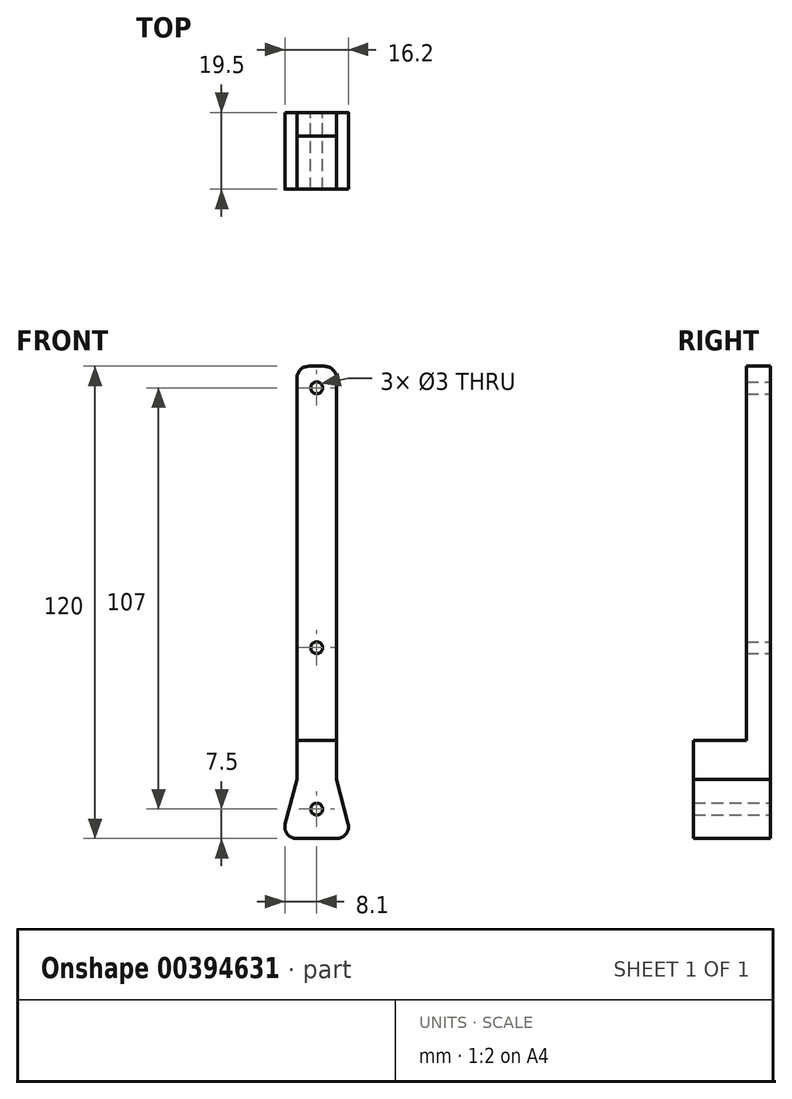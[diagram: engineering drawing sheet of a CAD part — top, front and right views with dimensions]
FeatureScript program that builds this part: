
annotation { "Feature Type Name" : "Feature", "Feature Type Description" : "" }
export const myFeature = defineFeature(function(context is Context, id is Id, definition is map)
    precondition{}
    {
        {
            var Q0;
            Q0=qCreatedBy(makeId("Front.planeOp"),FACE);
            var sketch = newSketch(context, id + "F0", { "sketchPlane" : qUnion([Q0])});
            skLineSegment(sketch, "E0", {"start": v(0, 0) * mm, "end": v(9, 0) * mm});
            skLineSegment(sketch, "E1", {"start": v(-1.18, 15) * mm, "end": v(3.08, 15) * mm, "construction": true});
            skLineSegment(sketch, "E2", {"start": v(5, 15) * mm, "end": v(9, 0) * mm});
            skLineSegment(sketch, "E3", {"start": v(5, 15) * mm, "end": v(5, 25) * mm});
            skLineSegment(sketch, "E4", {"start": v(5, 25) * mm, "end": v(0, 25) * mm});
            skLineSegment(sketch, "E5", {"start": v(0, 25) * mm, "end": v(0, 0) * mm});
            skLineSegment(sketch, "E6.MirrorCS", {"start": v(-5, 25) * mm, "end": v(0, 25) * mm});
            skLineSegment(sketch, "E7.MirrorCS", {"start": v(-5, 15) * mm, "end": v(-5, 25) * mm});
            skLineSegment(sketch, "E8.MirrorCS", {"start": v(-5, 15) * mm, "end": v(-9, 0) * mm});
            skLineSegment(sketch, "E9.MirrorCS", {"start": v(0, 0) * mm, "end": v(-9, 0) * mm});
            skLineSegment(sketch, "E10", {"start": v(7, 7.5) * mm, "end": v(-7, 7.5) * mm, "construction": true});
            skLineSegment(sketch, "E11.bottom", {"start": v(-5, 25) * mm, "end": v(5, 25) * mm});
            skLineSegment(sketch, "E11.top", {"start": v(-5, 120) * mm, "end": v(5, 120) * mm});
            skLineSegment(sketch, "E11.left", {"start": v(-5, 25) * mm, "end": v(-5, 120) * mm});
            skLineSegment(sketch, "E11.right", {"start": v(5, 25) * mm, "end": v(5, 120) * mm});
            skCircle(sketch, "E12", {"center": v(0, 7.5) * mm, "radius": 1.5 * mm});
            skCircle(sketch, "E13", {"center": v(0, 48.5) * mm, "radius": 1.5 * mm});
            skCircle(sketch, "E14", {"center": v(0, 114.5) * mm, "radius": 1.5 * mm});
            skSolve(sketch);
        }
        {
            var Q0;
            {var subQ1=sQuery(id+"F0.wireOp",EDGE,"E5");Q0=makeQuery(id+"F0.imprint","IMPRINT",FACE,{"disambiguationData":[TD([[makeQuery(id+"F0.imprint","IMPRINT",EDGE,{"derivedFrom":subQ1}),-1.0]])]});}
            var Q1;
            Q1=makeQuery(id+"F0.imprint","IMPRINT",FACE,{"disambiguationData":[TD([[makeQuery(id+"F0.imprint","IMPRINT",EDGE,{"derivedFrom":sQuery(id+"F0.wireOp",EDGE,"E0")}),1.0]])]});
            extrude(context, id + "F1", {"entities" : qUnion([Q0, Q1]), "depth" : 19.5 * mm});
        }
        {
            var Q0;
            Q0=makeQuery(id+"F0.imprint","IMPRINT",FACE,{"disambiguationData":[TD([[makeQuery(id+"F0.imprint","IMPRINT",EDGE,{"derivedFrom":sQuery(id+"F0.wireOp",EDGE,"E11.top")}),-1.0]])]});
            extrude(context, id + "F2", {"entities" : qUnion([Q0]), "operationType" : NewBodyOperationType.ADD, "depth" : 6 * mm});
        }
        {
            var Q0;
            Q0=makeQuery(id+"F2.opExtrude","SWEPT_EDGE",EDGE,{"disambiguationData":[OSD([sQuery(id+"F0.wireOp",EDGE,"E11.top"),sQuery(id+"F0.wireOp",EDGE,"E11.right")])]});
            var Q1;
            Q1=makeQuery(id+"F2.opExtrude","SWEPT_EDGE",EDGE,{"disambiguationData":[OSD([sQuery(id+"F0.wireOp",EDGE,"E11.top"),sQuery(id+"F0.wireOp",EDGE,"E11.left")])]});
            var Q2;
            Q2=makeQuery(id+"F1.opExtrude","SWEPT_EDGE",EDGE,{"disambiguationData":[OSD([sQuery(id+"F0.wireOp",EDGE,"E0"),sQuery(id+"F0.wireOp",EDGE,"E2")])]});
            var Q3;
            Q3=makeQuery(id+"F1.opExtrude","SWEPT_EDGE",EDGE,{"disambiguationData":[OSD([sQuery(id+"F0.wireOp",EDGE,"E8.MirrorCS"),sQuery(id+"F0.wireOp",EDGE,"E9.MirrorCS")])]});
            fillet(context, id + "F3", {"entities" : qUnion([Q0, Q1, Q2, Q3]), "radius" : 3 * mm, "tangentPropagation" : true, "allowEdgeOverflow" : false});
        }
    });
